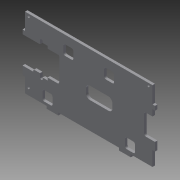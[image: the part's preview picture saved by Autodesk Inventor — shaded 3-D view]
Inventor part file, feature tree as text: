
AUTODESK INVENTOR PART (.ipt)
format: ipt  version: 2015 (Build 190159000, 159)  size: 326,144 bytes
history: native  units: mm
features: extrude x8, fillet x7, sketch x6
ambient origin geometry x8: Origin, YZ Plane, XZ Plane, XY Plane, X Axis, Y Axis, Z Axis, Center Point
bodies: Solid1 (feature_tree)
feature tree (21):
  extrude  "Extrusion1"  Depth=153.0mm
  extrude  "Extrusion2"  Depth=20.0mm
  extrude  "Extrusion3"  Depth=3.0mm
  extrude  "Extrusion6"  Depth=10.0mm
  fillet  "Fillet2"  Radius=3.0mm
  fillet  "Fillet4"  Radius=12.5mm
  sketch  "Sketch5"  dims[d3=3.0mm d4=20.0mm]
  extrude  "Extrusion8"  Depth=3.0mm TaperAngle=0.0deg
  fillet  "Fillet10"  Radius=20.0mm
  extrude  "Extrusion13"  Depth=3.0mm
  fillet  "Fillet11"  Radius=6.0mm
  fillet  "Fillet12"  Radius=20.0mm
  fillet  "Fillet13"  Radius=41.0mm
  fillet  "Fillet14"  Radius=6.0mm
  extrude  "Extrusion14"  Depth=26.0mm
  extrude  "Extrusion15"  Depth=48.0mm
  sketch  "Sketch1"  dims[d0=85.0mm d1=153.0mm]
  sketch  "Sketch6"  dims[d5=10.0mm d6=3.0mm]
  sketch  "Sketch10"  dims[d9=3.0mm d10=10.0mm d11=3.0mm d12=12.5mm]
  sketch  "Sketch11"  dims[d13=20.0mm d14=3.0mm d15=0.0mm d16=20.0mm]
  sketch  "Sketch12"  dims[d22=42.0mm d24=3.0mm d26=6.0mm d28=20.0mm d29=41.0mm d30=6.0mm d31=0.0mm d33=26.0mm d34=38.0mm d35=48.0mm d37=6.0mm d38=0.0mm d39=14.0mm d40=3.0mm d41=14.0mm d42=3.0mm d43=26.0mm d44=26.0mm d51=3.0mm d53=4.0mm d54=3.0mm d56=3.0mm d57=74.0mm d58=144.0mm d59=3.0mm d60=3.0mm d61=24.0mm d64=12.5mm d65=5.0mm d66=5.0mm d67=20.0mm d68=10.0mm d69=20.0mm d70=6.0mm d74=10.0mm d76=25.0mm d77=20.0mm d78=12.5mm d79=10.0mm d80=0.0mm d81=2.0mm d83=1.0mm d94=33.0mm d95=10.0mm d96=0.0mm d109=10.0mm d115=2.0mm d116=32.0mm d117=5.0mm d135=12.0mm d136=12.0mm d137=21.0mm d139=2.0mm d142=12.0mm d143=12.0mm d145=21.0mm d146=2.0mm d147=10.0mm d148=0.0mm d150=1.0mm d151=1.0mm d154=2.5mm d155=3.0mm d156=0.5mm d157=1.0mm d158=6.0mm d159=3.0mm d163=3.0mm d164=10.0mm d165=0.0mm d166=52.0mm d167=16.0mm d168=12.0mm d169=12.0mm d170=16.0mm d171=52.0mm d172=12.0mm d173=12.0mm d174=2.0mm d175=10.0mm d176=0.0mm d177=5.0mm d178=32.0mm]
